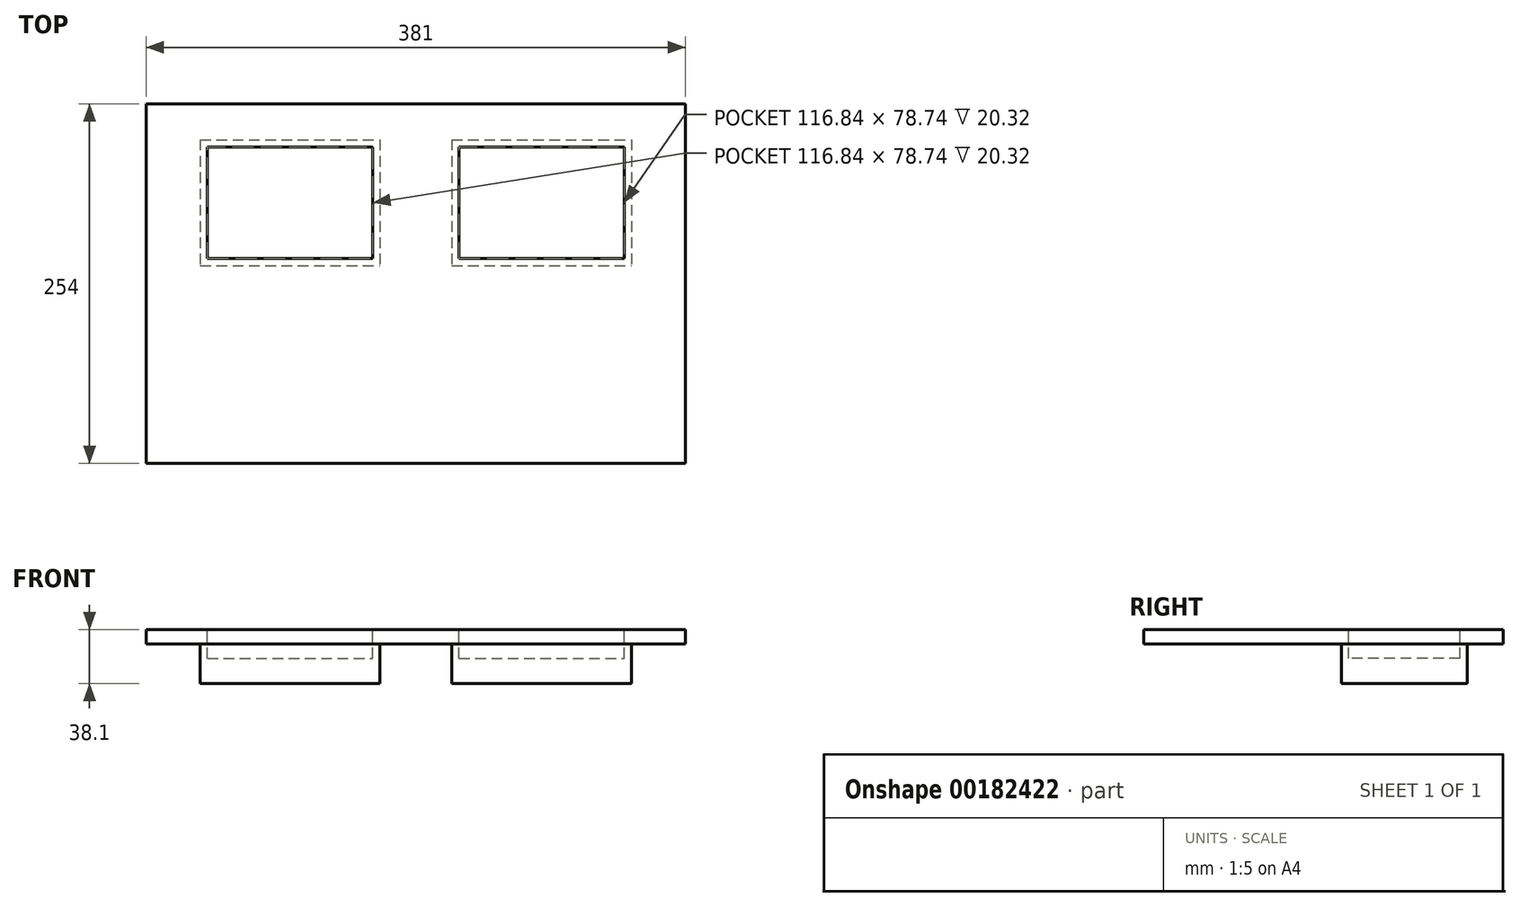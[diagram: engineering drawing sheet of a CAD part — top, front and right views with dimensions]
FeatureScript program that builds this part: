
annotation { "Feature Type Name" : "Feature", "Feature Type Description" : "" }
export const myFeature = defineFeature(function(context is Context, id is Id, definition is map)
    precondition{}
    {
        {
            var Q0;
            Q0=qCreatedBy(makeId("Top.planeOp"),FACE);
            var sketch = newSketch(context, id + "F0", { "sketchPlane" : qUnion([Q0])});
            skLineSegment(sketch, "E0.bottom", {"start": v(-189.54, -103.5) * mm, "end": v(191.46, -103.5) * mm});
            skLineSegment(sketch, "E0.top", {"start": v(-189.54, 150.5) * mm, "end": v(191.46, 150.5) * mm});
            skLineSegment(sketch, "E0.left", {"start": v(-189.54, -103.5) * mm, "end": v(-189.54, 150.5) * mm});
            skLineSegment(sketch, "E0.right", {"start": v(191.46, -103.5) * mm, "end": v(191.46, 150.5) * mm});
            skLineSegment(sketch, "E1.bottom", {"start": v(26.36, -89.04) * mm, "end": v(153.36, -89.04) * mm});
            skLineSegment(sketch, "E1.top", {"start": v(26.36, -0.14) * mm, "end": v(153.36, -0.14) * mm});
            skLineSegment(sketch, "E1.left", {"start": v(26.36, -89.04) * mm, "end": v(26.36, -0.14) * mm});
            skLineSegment(sketch, "E1.right", {"start": v(153.36, -89.04) * mm, "end": v(153.36, -0.14) * mm});
            skLineSegment(sketch, "E2.bottom", {"start": v(-151.44, -88.9) * mm, "end": v(-24.44, -88.9) * mm});
            skLineSegment(sketch, "E2.top", {"start": v(-151.44, 0) * mm, "end": v(-24.44, 0) * mm});
            skLineSegment(sketch, "E2.left", {"start": v(-151.44, -88.9) * mm, "end": v(-151.44, 0) * mm});
            skLineSegment(sketch, "E2.right", {"start": v(-24.44, -88.9) * mm, "end": v(-24.44, 0) * mm});
            skSolve(sketch);
        }
        {
            var Q0;
            Q0=makeQuery(id+"F0.imprint","IMPRINT",FACE,{"disambiguationData":[TD([[makeQuery(id+"F0.imprint","IMPRINT",EDGE,{"derivedFrom":sQuery(id+"F0.wireOp",EDGE,"E0.bottom")}),1.0]])]});
            var Q1;
            Q1=makeQuery(id+"F0.imprint","IMPRINT",FACE,{"disambiguationData":[TD([[makeQuery(id+"F0.imprint","IMPRINT",EDGE,{"derivedFrom":sQuery(id+"F0.wireOp",EDGE,"E2.bottom")}),1.0]])]});
            var Q2;
            Q2=makeQuery(id+"F0.imprint","IMPRINT",FACE,{"disambiguationData":[TD([[makeQuery(id+"F0.imprint","IMPRINT",EDGE,{"derivedFrom":sQuery(id+"F0.wireOp",EDGE,"E1.bottom")}),1.0]])]});
            extrude(context, id + "F1", {"entities" : qUnion([Q0, Q1, Q2]), "depth" : 10.16 * mm});
        }
        {
            var Q0;
            Q0=makeQuery(id+"F1.opExtrude","CAP_FACE",FACE,{"disambiguationData":[OSD([sQuery(id+"F0.wireOp",EDGE,"E0.bottom"),sQuery(id+"F0.wireOp",EDGE,"E0.top"),sQuery(id+"F0.wireOp",EDGE,"E0.left"),sQuery(id+"F0.wireOp",EDGE,"E0.right")])],"isStart":false});
            var sketch = newSketch(context, id + "F2", { "sketchPlane" : qUnion([Q0])});
            skLineSegment(sketch, "E3.bottom", {"start": v(-151.44, 125.1) * mm, "end": v(-24.44, 125.1) * mm});
            skLineSegment(sketch, "E3.top", {"start": v(-151.44, 36.2) * mm, "end": v(-24.44, 36.2) * mm});
            skLineSegment(sketch, "E3.left", {"start": v(-151.44, 125.1) * mm, "end": v(-151.44, 36.2) * mm});
            skLineSegment(sketch, "E3.right", {"start": v(-24.44, 125.1) * mm, "end": v(-24.44, 36.2) * mm});
            skLineSegment(sketch, "E4.bottom", {"start": v(26.36, 125.1) * mm, "end": v(153.36, 125.1) * mm});
            skLineSegment(sketch, "E4.top", {"start": v(26.36, 36.2) * mm, "end": v(153.36, 36.2) * mm});
            skLineSegment(sketch, "E4.left", {"start": v(26.36, 125.1) * mm, "end": v(26.36, 36.2) * mm});
            skLineSegment(sketch, "E4.right", {"start": v(153.36, 125.1) * mm, "end": v(153.36, 36.2) * mm});
            skSolve(sketch);
        }
        {
            var Q0;
            Q0=makeQuery(id+"F2.imprint","IMPRINT",FACE,{"disambiguationData":[TD([[makeQuery(id+"F2.imprint","IMPRINT",EDGE,{"derivedFrom":sQuery(id+"F2.wireOp",EDGE,"E3.bottom")}),-1.0]])]});
            var Q1;
            Q1=makeQuery(id+"F2.imprint","IMPRINT",FACE,{"disambiguationData":[TD([[makeQuery(id+"F2.imprint","IMPRINT",EDGE,{"derivedFrom":sQuery(id+"F2.wireOp",EDGE,"E4.bottom")}),-1.0]])]});
            extrude(context, id + "F3", {"entities" : qUnion([Q0, Q1]), "operationType" : NewBodyOperationType.ADD, "oppositeDirection" : true, "depth" : 38.1 * mm});
        }
        {
            var Q0;
            Q0=makeQuery(id+"F1.opExtrude","CAP_FACE",FACE,{"disambiguationData":[OSD([sQuery(id+"F0.wireOp",EDGE,"E0.bottom"),sQuery(id+"F0.wireOp",EDGE,"E0.top"),sQuery(id+"F0.wireOp",EDGE,"E0.left"),sQuery(id+"F0.wireOp",EDGE,"E0.right")])],"isStart":false});
            var sketch = newSketch(context, id + "F4", { "sketchPlane" : qUnion([Q0])});
            skLineSegment(sketch, "E5.bottom", {"start": v(-146.36, 120.01) * mm, "end": v(-29.52, 120.01) * mm});
            skLineSegment(sketch, "E5.top", {"start": v(-146.36, 41.27) * mm, "end": v(-29.52, 41.27) * mm});
            skLineSegment(sketch, "E5.left", {"start": v(-146.36, 120.01) * mm, "end": v(-146.36, 41.27) * mm});
            skLineSegment(sketch, "E5.right", {"start": v(-29.52, 120.01) * mm, "end": v(-29.52, 41.27) * mm});
            skLineSegment(sketch, "E6.bottom", {"start": v(31.44, 120.01) * mm, "end": v(148.28, 120.01) * mm});
            skLineSegment(sketch, "E6.top", {"start": v(31.44, 41.27) * mm, "end": v(148.28, 41.27) * mm});
            skLineSegment(sketch, "E6.left", {"start": v(31.44, 120.01) * mm, "end": v(31.44, 41.27) * mm});
            skLineSegment(sketch, "E6.right", {"start": v(148.28, 120.01) * mm, "end": v(148.28, 41.27) * mm});
            skSolve(sketch);
        }
        {
            var Q0;
            Q0=makeQuery(id+"F4.imprint","IMPRINT",FACE,{"disambiguationData":[TD([[makeQuery(id+"F4.imprint","IMPRINT",EDGE,{"derivedFrom":sQuery(id+"F4.wireOp",EDGE,"E5.bottom")}),-1.0]])]});
            var Q1;
            Q1=makeQuery(id+"F4.imprint","IMPRINT",FACE,{"disambiguationData":[TD([[makeQuery(id+"F4.imprint","IMPRINT",EDGE,{"derivedFrom":sQuery(id+"F4.wireOp",EDGE,"E6.bottom")}),-1.0]])]});
            extrude(context, id + "F5", {"entities" : qUnion([Q0, Q1]), "operationType" : NewBodyOperationType.REMOVE, "oppositeDirection" : true, "depth" : 20.32 * mm});
        }
    });
